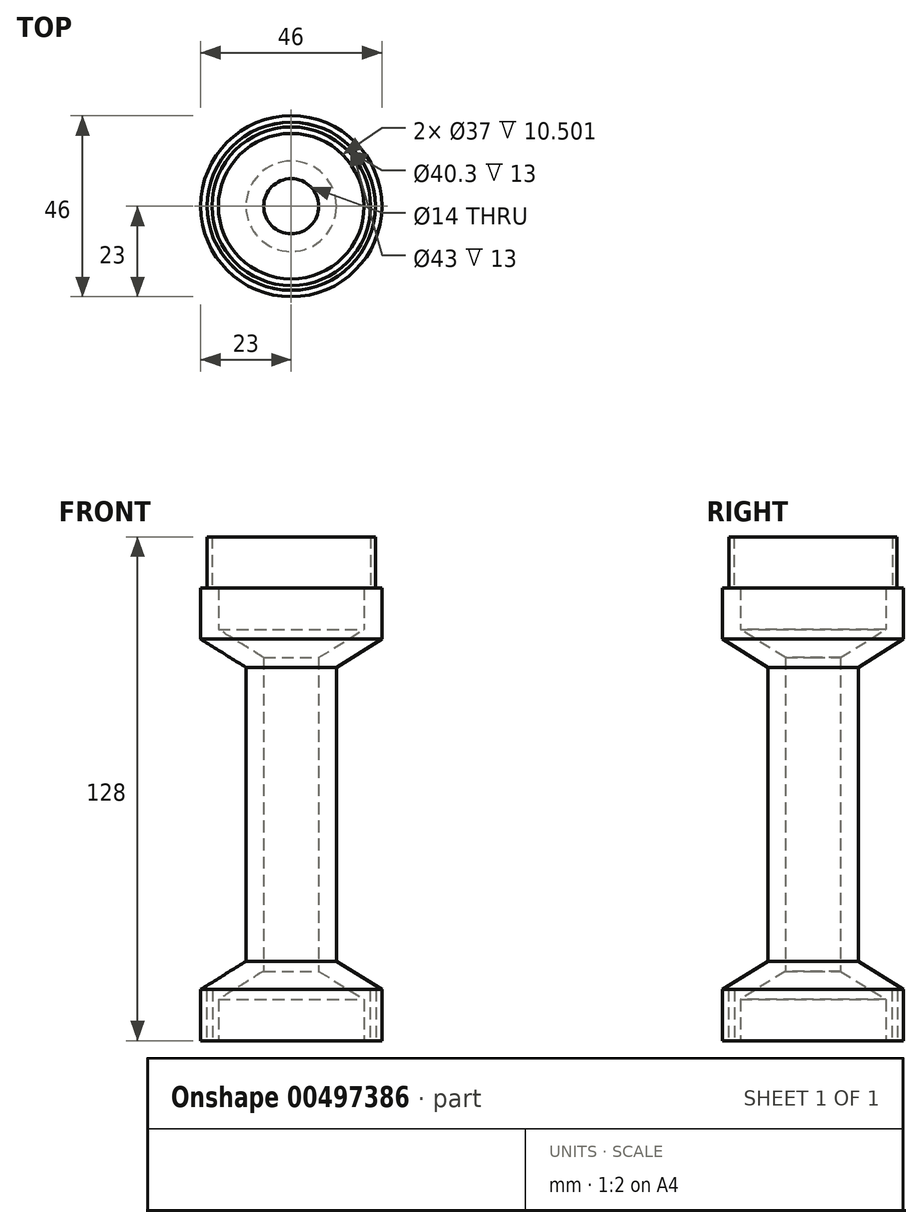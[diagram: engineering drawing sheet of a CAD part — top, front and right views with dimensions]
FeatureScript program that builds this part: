
annotation { "Feature Type Name" : "Feature", "Feature Type Description" : "" }
export const myFeature = defineFeature(function(context is Context, id is Id, definition is map)
    precondition{}
    {
        {
            var Q0;
            Q0=qCreatedBy(makeId("Front.planeOp"),FACE);
            var sketch = newSketch(context, id + "F0", { "sketchPlane" : qUnion([Q0])});
            skLineSegment(sketch, "E0", {"start": v(0, 0) * mm, "end": v(23, 0) * mm});
            skLineSegment(sketch, "E1.bottom", {"start": v(23, 0) * mm, "end": v(21.5, 0) * mm});
            skLineSegment(sketch, "E1.top", {"start": v(23, -13) * mm, "end": v(21.5, -13) * mm});
            skLineSegment(sketch, "E1.left", {"start": v(23, 0) * mm, "end": v(23, -13) * mm});
            skLineSegment(sketch, "E1.right", {"start": v(21.5, 0) * mm, "end": v(21.5, -13) * mm});
            skLineSegment(sketch, "E2.bottom", {"start": v(21.5, 0) * mm, "end": v(20, 0) * mm});
            skLineSegment(sketch, "E2.top", {"start": v(21.5, -13) * mm, "end": v(20, -13) * mm});
            skLineSegment(sketch, "E2.right", {"start": v(20, 0) * mm, "end": v(20, -13) * mm});
            skLineSegment(sketch, "E3.bottom", {"start": v(20, -13) * mm, "end": v(18.5, -13) * mm});
            skLineSegment(sketch, "E3.top", {"start": v(20, 0) * mm, "end": v(18.5, 0) * mm});
            skLineSegment(sketch, "E3.left", {"start": v(20, -13) * mm, "end": v(20, 0) * mm});
            skLineSegment(sketch, "E3.right", {"start": v(18.5, -13) * mm, "end": v(18.5, 0) * mm});
            skLineSegment(sketch, "E4.bottom", {"start": v(23, 0) * mm, "end": v(0, 0) * mm});
            skLineSegment(sketch, "E4.top", {"start": v(23, 102) * mm, "end": v(0, 102) * mm});
            skLineSegment(sketch, "E4.left", {"start": v(23, 0) * mm, "end": v(23, 102) * mm});
            skLineSegment(sketch, "E4.right", {"start": v(0, 0) * mm, "end": v(0, 102) * mm});
            skLineSegment(sketch, "E5.bottom", {"start": v(21.35, 102) * mm, "end": v(20.15, 102) * mm});
            skLineSegment(sketch, "E5.top", {"start": v(21.35, 115) * mm, "end": v(20.15, 115) * mm});
            skLineSegment(sketch, "E5.left", {"start": v(21.35, 102) * mm, "end": v(21.35, 115) * mm});
            skLineSegment(sketch, "E5.right", {"start": v(20.15, 102) * mm, "end": v(20.15, 115) * mm});
            skLineSegment(sketch, "E6", {"start": v(0, 44.5) * mm, "end": v(23, 44.5) * mm});
            skLineSegment(sketch, "E7.0", {"start": v(18.5, 0) * mm, "end": v(18.5, 102) * mm});
            skLineSegment(sketch, "E8", {"start": v(23, 0) * mm, "end": v(11.5, 7.16) * mm});
            skPoint(sketch, "E8.endSnap0", {"position": v(11.5, 44.5) * mm});
            skLineSegment(sketch, "E9", {"start": v(11.5, 7.16) * mm, "end": v(11.5, 44.5) * mm});
            skLineSegment(sketch, "E10.0", {"start": v(7, 4.66) * mm, "end": v(7, 44.5) * mm});
            skLineSegment(sketch, "E10.1", {"start": v(20.62, -3.82) * mm, "end": v(7, 4.66) * mm});
            skLineSegment(sketch, "E11.MirrorCS", {"start": v(11.5, 81.84) * mm, "end": v(11.5, 44.5) * mm});
            skLineSegment(sketch, "E12.MirrorCS", {"start": v(7, 84.34) * mm, "end": v(7, 44.5) * mm});
            skLineSegment(sketch, "E13.MirrorCS", {"start": v(20.62, 92.82) * mm, "end": v(7, 84.34) * mm});
            skLineSegment(sketch, "E14.MirrorCS", {"start": v(23, 89) * mm, "end": v(11.5, 81.84) * mm});
            skSolve(sketch);
        }
        {
            var Q0;
            Q0=makeQuery(id+"F0.imprint","IMPRINT",FACE,{"disambiguationData":[TD([[makeQuery(id+"F0.imprint","IMPRINT",EDGE,{"derivedFrom":sQuery(id+"F0.wireOp",EDGE,"E1.top")}),-1.0]])]});
            var Q1;
            {var subQ0=sQuery(id+"F0.wireOp",EDGE,"E3.bottom");Q1=makeQuery(id+"F0.imprint","IMPRINT",FACE,{"disambiguationData":[TD([[makeQuery(id+"F0.imprint","IMPRINT",EDGE,{"derivedFrom":subQ0}),-1.0]])]});}
            var Q2;
            {var subQ1=sQuery(id+"F0.wireOp",EDGE,"E0");var subQ5=makeQuery(id+"F0.imprint","INTERSECT",VERTEX,{"derivedFrom":[subQ1,sQuery(id+"F0.wireOp",EDGE,"E1.right")]});Q2=makeQuery(id+"F0.imprint","IMPRINT",FACE,{"disambiguationData":[TD([[makeQuery(id+"F0.imprint","IMPRINT",EDGE,{"disambiguationData":[TD([[subQ5,1.0]])],"derivedFrom":subQ1}),1.0]])]});}
            var Q3;
            {var subQ0=sQuery(id+"F0.wireOp",EDGE,"E4.top");var subQ5=sQuery(id+"F0.wireOp",EDGE,"E4.left");var subQ6=makeQuery(id+"F0.imprint","INTERSECT",VERTEX,{"derivedFrom":[subQ0,subQ5]});Q3=makeQuery(id+"F0.imprint","IMPRINT",FACE,{"disambiguationData":[TD([[makeQuery(id+"F0.imprint","IMPRINT",EDGE,{"disambiguationData":[TD([[subQ6,-1.0]])],"derivedFrom":subQ0}),1.0]])]});}
            var Q4;
            Q4=makeQuery(id+"F0.imprint","IMPRINT",FACE,{"disambiguationData":[TD([[makeQuery(id+"F0.imprint","IMPRINT",EDGE,{"derivedFrom":sQuery(id+"F0.wireOp",EDGE,"E5.top")}),1.0]])]});
            var Q5;
            {var subQ0=sQuery(id+"F0.wireOp",EDGE,"E11.MirrorCS");Q5=makeQuery(id+"F0.imprint","IMPRINT",FACE,{"disambiguationData":[TD([[makeQuery(id+"F0.imprint","IMPRINT",EDGE,{"derivedFrom":subQ0}),-1.0]])]});}
            var Q6;
            {var subQ3=sQuery(id+"F0.wireOp",EDGE,"E9");Q6=makeQuery(id+"F0.imprint","IMPRINT",FACE,{"disambiguationData":[TD([[makeQuery(id+"F0.imprint","IMPRINT",EDGE,{"derivedFrom":subQ3}),1.0]])]});}
            var Q7;
            {var subQ1=sQuery(id+"F0.wireOp",EDGE,"E0");var subQ3=sQuery(id+"F0.wireOp",EDGE,"E10.1");var subQ4=makeQuery(id+"F0.imprint","INTERSECT",VERTEX,{"derivedFrom":[subQ1,subQ3]});Q7=makeQuery(id+"F0.imprint","IMPRINT",FACE,{"disambiguationData":[TD([[makeQuery(id+"F0.imprint","IMPRINT",EDGE,{"disambiguationData":[TD([[subQ4,1.0]])],"derivedFrom":subQ3}),-1.0]])]});}
            var Q8;
            {var subQ3=sQuery(id+"F0.wireOp",EDGE,"E2.right");var subQ5=sQuery(id+"F0.wireOp",EDGE,"E10.1");var subQ6=makeQuery(id+"F0.imprint","INTERSECT",VERTEX,{"derivedFrom":[subQ3,subQ5]});Q8=makeQuery(id+"F0.imprint","IMPRINT",FACE,{"disambiguationData":[TD([[makeQuery(id+"F0.imprint","IMPRINT",EDGE,{"disambiguationData":[TD([[subQ6,1.0]])],"derivedFrom":subQ3}),-1.0]])]});}
            var Q9;
            Q9=sQuery(id+"F0.wireOp",EDGE,"E4.right");
            revolve(context, id + "F1", {"entities" : qUnion([Q0, Q1, Q2, Q3, Q4, Q5, Q6, Q7, Q8]), "axis" : qUnion([Q9]), "revolveType" : RevolveType.FULL});
        }
    });
